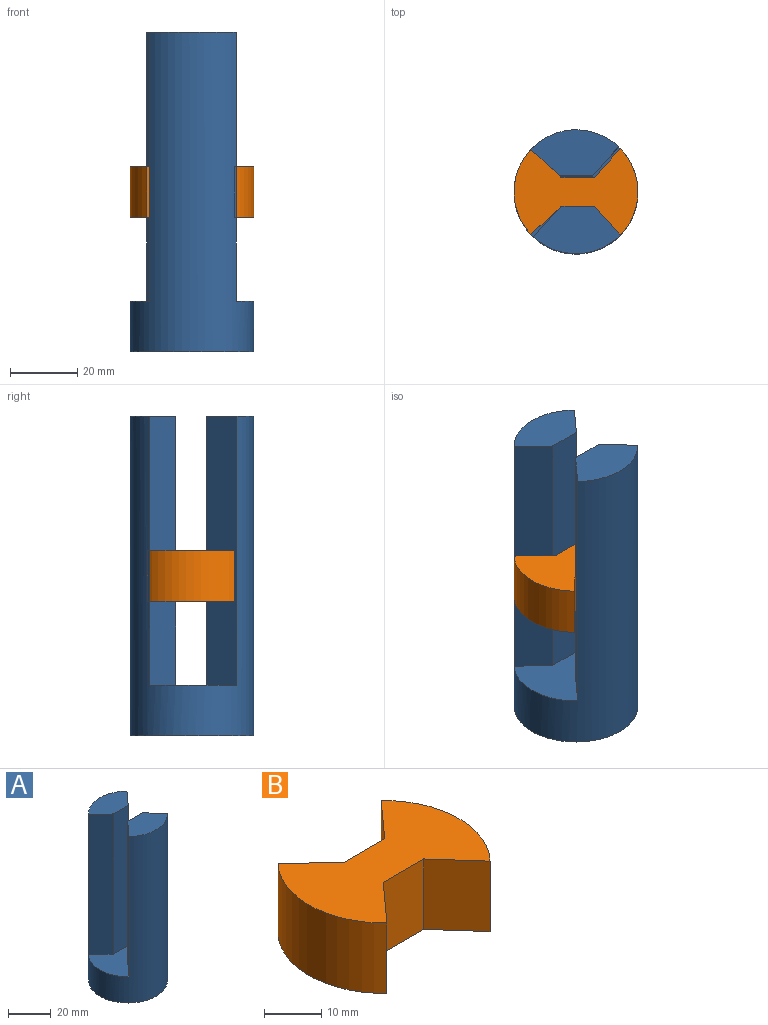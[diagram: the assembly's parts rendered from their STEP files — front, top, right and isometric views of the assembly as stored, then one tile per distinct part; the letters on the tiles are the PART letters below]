
ASSEMBLY  parts=2 mates=1
PART A: 11 faces, bbox 36.9x36.9x95 mm
  f0: plane 36.89x26.78mm, normal (0,0,1), area 569.9mm2, adj f1,f3,f4,f5,f7,f8,f9
  f1: cylinder r=18.45mm len=95mm, axis (0,0,1), area 6355.8mm2, adj f0,f2,f3,f4,f6,f7,f8,f10
  f2: plane 36.89x36.89mm, normal (0,0,-1), area 1068.9mm2, adj f1
  f3: plane 80x8.57mm, normal (0.74,-0.67,0), area 922.1mm2, adj f0,f1,f5,f6
  f4: plane 80x8.46mm, normal (-0.68,-0.73,0), area 921.3mm2, adj f0,f1,f5,f6
  f5: plane 80x9.97mm, normal (0,-1,0), area 797.5mm2, adj f0,f3,f4,f6
  f6: plane 26.13x13.63mm, normal (0,0,1), area 245.9mm2, adj f1,f3,f4,f5
  f7: plane 80x9.12mm, normal (-0.74,0.67,0), area 981.2mm2, adj f0,f1,f9,f10
  f8: plane 80x8.62mm, normal (0.75,0.67,0), area 924.3mm2, adj f0,f1,f9,f10
  f9: plane 80x9.97mm, normal (0,1,0), area 797.5mm2, adj f0,f7,f8,f10
  f10: plane 25.86x14.17mm, normal (0,0,1), area 253.1mm2, adj f1,f7,f8,f9
PART B: 10 faces, bbox 36.9x26.8x15 mm
  f0: cylinder r=18.45mm len=26.29mm, axis (0,0,-1), area 439mm2, adj f1,f7,f8,f9
  f1: plane 15x8.57mm, normal (-0.74,0.67,0), area 172.9mm2, adj f0,f2,f8,f9
  f2: plane 15x9.97mm, normal (0,1,0), area 149.5mm2, adj f1,f3,f8,f9
  f3: plane 15x8.46mm, normal (0.68,0.73,0), area 172.7mm2, adj f2,f4,f8,f9
  f4: cylinder r=18.45mm len=26.03mm, axis (0,0,-1), area 433.7mm2, adj f3,f5,f8,f9
  f5: plane 15x9.12mm, normal (0.74,-0.67,0), area 184mm2, adj f4,f6,f8,f9
  f6: plane 15x9.97mm, normal (0,-1,0), area 149.5mm2, adj f5,f7,f8,f9
  f7: plane 15x8.62mm, normal (-0.75,-0.67,0), area 173.3mm2, adj f0,f6,f8,f9
  f8: plane 36.89x26.78mm, normal (0,0,1), area 569.9mm2, adj f0,f1,f2,f3,f4,f5,f6,f7
  f9: plane 36.89x26.78mm, normal (0,0,-1), area 569.9mm2, adj f0,f1,f2,f3,f4,f5,f6,f7
PLACE A rot(axis=(-0.49,-0.66,-0.57),0deg) t=(-11.26,0.71,3.3)mm
PLACE B rot(axis=(1,0,0),180deg) t=(-11.26,0.71,43.3)mm
MATE slider B.f0 <-> A.f1  axis (0,0,1) through (-11.26,0.71,35.8)mm
